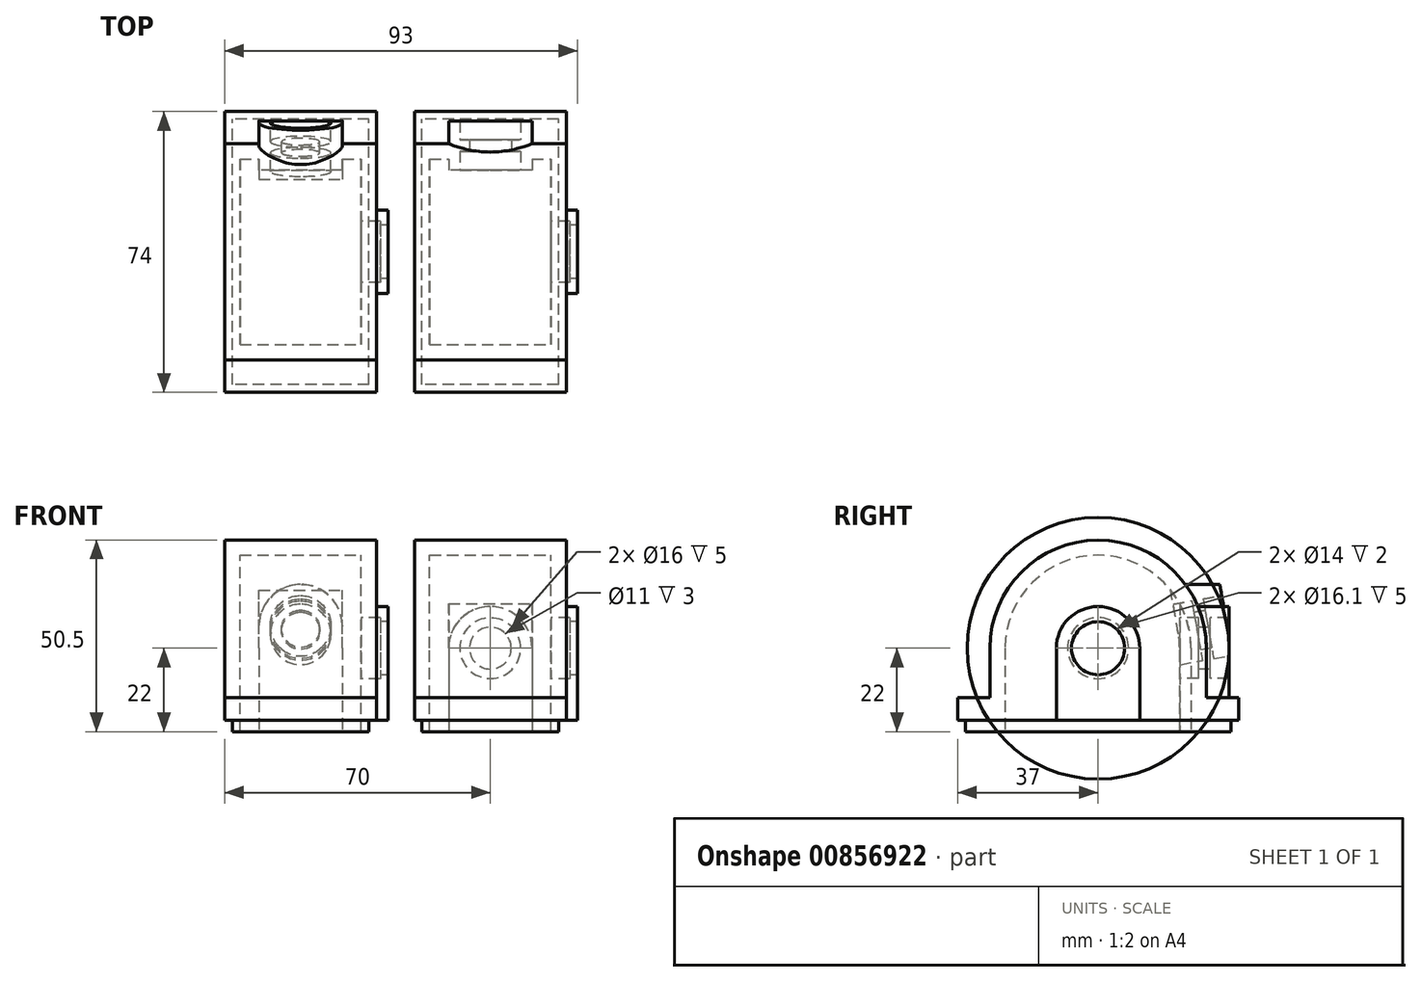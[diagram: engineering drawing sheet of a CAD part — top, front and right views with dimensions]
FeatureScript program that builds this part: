
annotation { "Feature Type Name" : "Feature", "Feature Type Description" : "" }
export const myFeature = defineFeature(function(context is Context, id is Id, definition is map)
    precondition{}
    {
        {
            var Q0;
            Q0=qCreatedBy(makeId("Right.planeOp"),FACE);
            var sketch = newSketch(context, id + "F0", { "sketchPlane" : qUnion([Q0])});
            skArc(sketch, "E0", {"start": v(28.5, 22) * mm, "mid": v(0, 50.5) * mm, "end": v(-28.5, 22) * mm});
            skLineSegment(sketch, "E1", {"start": v(-28.5, 22) * mm, "end": v(28.5, 22) * mm, "construction": true});
            skLineSegment(sketch, "E2", {"start": v(-28.5, 22) * mm, "end": v(-28.5, 9) * mm});
            skLineSegment(sketch, "E3", {"start": v(28.5, 22) * mm, "end": v(28.5, 9) * mm});
            skLineSegment(sketch, "E4.top", {"start": v(37, 9) * mm, "end": v(28.5, 9) * mm});
            skLineSegment(sketch, "E4.left", {"start": v(37, 0) * mm, "end": v(37, 9) * mm});
            skLineSegment(sketch, "E4.right", {"start": v(-37, 0) * mm, "end": v(-37, 9) * mm});
            skPoint(sketch, "E4.middle", {"position": v(0, 4.5) * mm});
            skLineSegment(sketch, "E5.trimOffspring", {"start": v(-28.5, 9) * mm, "end": v(-37, 9) * mm});
            skLineSegment(sketch, "E6", {"start": v(-37, 0) * mm, "end": v(37, 0) * mm});
            skSolve(sketch);
        }
        {
            var Q0;
            Q0 = qSketchRegion(id + "F0", true);
            extrude(context, id + "F1", {"entities" : qUnion([Q0]), "depth" : 40 * mm, "offsetDistance" : 25 * mm, "symmetric" : true});
        }
        {
            var Q0;
            Q0=qCreatedBy(makeId("Right.planeOp"),FACE);
            var sketch = newSketch(context, id + "F2", { "sketchPlane" : qUnion([Q0])});
            skArc(sketch, "E7", {"start": v(24.5, 22) * mm, "mid": v(0, 46.5) * mm, "end": v(-24.5, 22) * mm});
            skLineSegment(sketch, "E8", {"start": v(-24.5, 22) * mm, "end": v(24.5, 22) * mm, "construction": true});
            skLineSegment(sketch, "E9", {"start": v(-24.5, 22) * mm, "end": v(-24.5, 0) * mm});
            skLineSegment(sketch, "E10", {"start": v(-24.5, 0) * mm, "end": v(24.5, 0) * mm});
            skLineSegment(sketch, "E11", {"start": v(24.5, 0) * mm, "end": v(24.5, 22) * mm});
            skSolve(sketch);
        }
        {
            var Q0;
            Q0 = qSketchRegion(id + "F2", true);
            extrude(context, id + "F3", {"entities" : qUnion([Q0]), "operationType" : NewBodyOperationType.REMOVE, "oppositeDirection" : true, "depth" : 32 * mm, "offsetDistance" : 25 * mm, "symmetric" : true});
        }
        {
            var Q0;
            Q0=makeQuery(id+"F1.opExtrude","CAP_FACE",FACE,{"disambiguationData":[OSD([sQuery(id+"F0.wireOp",EDGE,"E0"),sQuery(id+"F0.wireOp",EDGE,"E2"),sQuery(id+"F0.wireOp",EDGE,"E3"),sQuery(id+"F0.wireOp",EDGE,"E4.top"),sQuery(id+"F0.wireOp",EDGE,"E4.left"),sQuery(id+"F0.wireOp",EDGE,"E4.right"),sQuery(id+"F0.wireOp",EDGE,"E5.trimOffspring"),sQuery(id+"F0.wireOp",EDGE,"E6")])],"isStart":false});
            var sketch = newSketch(context, id + "F4", { "sketchPlane" : qUnion([Q0])});
            skArc(sketch, "E12", {"start": v(11, 22) * mm, "mid": v(0, 33) * mm, "end": v(-11, 22) * mm});
            skLineSegment(sketch, "E13", {"start": v(-11, 22) * mm, "end": v(-11, 0) * mm});
            skLineSegment(sketch, "E14", {"start": v(-11, 0) * mm, "end": v(11, 0) * mm});
            skLineSegment(sketch, "E15", {"start": v(11, 0) * mm, "end": v(11, 22) * mm});
            skSolve(sketch);
        }
        {
            var Q0;
            Q0 = qSketchRegion(id + "F4", true);
            extrude(context, id + "F5", {"entities" : qUnion([Q0]), "operationType" : NewBodyOperationType.ADD, "depth" : 3 * mm, "offsetDistance" : 25 * mm});
        }
        {
            var Q0;
            Q0=qCreatedBy(makeId("Front.planeOp"),FACE);
            var sketch = newSketch(context, id + "F6", { "sketchPlane" : qUnion([Q0])});
            skLineSegment(sketch, "E16", {"start": v(42.03, 22) * mm, "end": v(7.34, 22) * mm, "construction": true});
            skLineSegment(sketch, "E17", {"start": v(16, 22) * mm, "end": v(16, 30.05) * mm});
            skLineSegment(sketch, "E18", {"start": v(16, 30.05) * mm, "end": v(21, 30.05) * mm});
            skLineSegment(sketch, "E19", {"start": v(21, 30.05) * mm, "end": v(21, 29) * mm});
            skLineSegment(sketch, "E20", {"start": v(21, 29) * mm, "end": v(23, 29) * mm});
            skLineSegment(sketch, "E21", {"start": v(23, 29) * mm, "end": v(23, 22) * mm});
            skLineSegment(sketch, "E22", {"start": v(23, 22) * mm, "end": v(16, 22) * mm});
            skLineSegment(sketch, "E23", {"start": v(16, 22) * mm, "end": v(23, 22) * mm});
            skSolve(sketch);
        }
        {
            var Q0;
            Q0 = qSketchRegion(id + "F6", true);
            var Q1;
            Q1=sQuery(id+"F6.wireOp",EDGE,"E16");
            revolve(context, id + "F7", {"operationType" : NewBodyOperationType.REMOVE, "surfaceOperationType" : NewSurfaceOperationType.NEW, "entities" : qUnion([Q0]), "axis" : qUnion([Q1]), "revolveType" : RevolveType.FULL, "oppositeDirection" : true});
        }
        {
            var Q0;
            {var subQ0=sQuery(id+"F4.wireOp",EDGE,"E14");Q0=makeQuery(id+"Fj3ByAB7jm97h4G_1.1.F5.boolean.opBoolean","MERGE",FACE,{"derivedFrom":[makeQuery(id+"F5.boolean.opBoolean","MERGE",FACE,{"derivedFrom":[makeQuery(id+"F1.opExtrude","SWEPT_FACE",FACE,{"disambiguationData":[OSD([sQuery(id+"F0.wireOp",EDGE,"E6")])]}),makeQuery(id+"F5.opExtrude","SWEPT_FACE",FACE,{"disambiguationData":[OSD([subQ0])]})]}),makeQuery(id+"Fj3ByAB7jm97h4G_1.1.F5.opExtrude","SWEPT_FACE",FACE,{"disambiguationData":[OSD([subQ0])]})]});}
            var sketch = newSketch(context, id + "F8", { "sketchPlane" : qUnion([Q0])});
            skLineSegment(sketch, "E24.bottom", {"start": v(18, 35) * mm, "end": v(-18, 35) * mm});
            skLineSegment(sketch, "E24.top", {"start": v(18, -35) * mm, "end": v(-18, -35) * mm});
            skLineSegment(sketch, "E24.left", {"start": v(18, 35) * mm, "end": v(18, -35) * mm});
            skLineSegment(sketch, "E24.right", {"start": v(-18, 35) * mm, "end": v(-18, -35) * mm});
            skPoint(sketch, "E24.middle", {"position": v(0, 0) * mm});
            skLineSegment(sketch, "E25.0.0", {"start": v(-20, 37) * mm, "end": v(-20, 11) * mm});
            skLineSegment(sketch, "E25.0.1", {"start": v(-20, 11) * mm, "end": v(-23, 11) * mm});
            skLineSegment(sketch, "E25.0.2", {"start": v(-23, 11) * mm, "end": v(-23, -11) * mm});
            skLineSegment(sketch, "E25.0.3", {"start": v(-23, -11) * mm, "end": v(-20, -11) * mm});
            skLineSegment(sketch, "E25.0.4", {"start": v(-20, -11) * mm, "end": v(-20, -37) * mm});
            skLineSegment(sketch, "E25.0.5", {"start": v(-20, -37) * mm, "end": v(20, -37) * mm});
            skLineSegment(sketch, "E25.0.6", {"start": v(20, -37) * mm, "end": v(20, -11) * mm});
            skLineSegment(sketch, "E25.0.7", {"start": v(20, -11) * mm, "end": v(23, -11) * mm});
            skLineSegment(sketch, "E25.0.8", {"start": v(23, -11) * mm, "end": v(23, 11) * mm});
            skLineSegment(sketch, "E25.0.9", {"start": v(23, 11) * mm, "end": v(20, 11) * mm});
            skLineSegment(sketch, "E25.0.10", {"start": v(20, 11) * mm, "end": v(20, 37) * mm});
            skLineSegment(sketch, "E25.0.11", {"start": v(20, 37) * mm, "end": v(-20, 37) * mm});
            skSolve(sketch);
        }
        {
            var Q0;
            Q0 = qSketchRegion(id + "F8", true);
            extrude(context, id + "F9", {"entities" : qUnion([Q0]), "operationType" : NewBodyOperationType.REMOVE, "oppositeDirection" : true, "depth" : 3 * mm, "offsetDistance" : 25 * mm});
        }
        {
            var Q0;
            Q0=makeQuery(id+"F1.opExtrude","SWEPT_BODY",BODY,{"disambiguationData":[OSD([sQuery(id+"F0.wireOp",EDGE,"E0"),sQuery(id+"F0.wireOp",EDGE,"E2"),sQuery(id+"F0.wireOp",EDGE,"E3"),sQuery(id+"F0.wireOp",EDGE,"E4.top"),sQuery(id+"F0.wireOp",EDGE,"E4.left"),sQuery(id+"F0.wireOp",EDGE,"E4.right"),sQuery(id+"F0.wireOp",EDGE,"E5.trimOffspring"),sQuery(id+"F0.wireOp",EDGE,"E6")])]});
            transform(context, id + "F10", {"entities" : qUnion([Q0]), "transformType" : TransformType.TRANSLATION_3D, "dx" : 50 * mm, "dy" : 0 * mm, "dz" : 0 * mm, "makeCopy" : true});
        }
        {
            var Q0;
            Q0=makeQuery(id+"F10.opPattern","COPY",FACE,{"derivedFrom":makeQuery(id+"F1.opExtrude","CAP_FACE",FACE,{"disambiguationData":[OSD([sQuery(id+"F0.wireOp",EDGE,"E0"),sQuery(id+"F0.wireOp",EDGE,"E2"),sQuery(id+"F0.wireOp",EDGE,"E3"),sQuery(id+"F0.wireOp",EDGE,"E4.top"),sQuery(id+"F0.wireOp",EDGE,"E4.left"),sQuery(id+"F0.wireOp",EDGE,"E4.right"),sQuery(id+"F0.wireOp",EDGE,"E5.trimOffspring"),sQuery(id+"F0.wireOp",EDGE,"E6")])],"isStart":false}),"instanceName":"1"});
            var Q1;
            Q1=makeQuery(id+"F10.opPattern","COPY",FACE,{"derivedFrom":makeQuery(id+"F1.opExtrude","CAP_FACE",FACE,{"disambiguationData":[OSD([sQuery(id+"F0.wireOp",EDGE,"E0"),sQuery(id+"F0.wireOp",EDGE,"E2"),sQuery(id+"F0.wireOp",EDGE,"E3"),sQuery(id+"F0.wireOp",EDGE,"E4.top"),sQuery(id+"F0.wireOp",EDGE,"E4.left"),sQuery(id+"F0.wireOp",EDGE,"E4.right"),sQuery(id+"F0.wireOp",EDGE,"E5.trimOffspring"),sQuery(id+"F0.wireOp",EDGE,"E6")])],"isStart":true}),"instanceName":"1"});
            cPlane(context, id + "F11", {"entities" : qUnion([Q0, Q1]), "cplaneType" : CPlaneType.MID_PLANE, "offset" : 25 * mm, "width" : 150 * mm, "height" : 150 * mm});
        }
        {
            var Q0;
            Q0=qCreatedBy(id+"F11.planeOp",FACE);
            var sketch = newSketch(context, id + "F12", { "sketchPlane" : qUnion([Q0])});
            skLineSegment(sketch, "E26", {"start": v(21.5, 0) * mm, "end": v(21.5, 33) * mm});
            skLineSegment(sketch, "E27", {"start": v(24.84, 33) * mm, "end": v(34.5, 33) * mm});
            skLineSegment(sketch, "E28", {"start": v(34.5, 33) * mm, "end": v(34.5, 0) * mm});
            skLineSegment(sketch, "E29", {"start": v(34.5, 0) * mm, "end": v(21.5, 0) * mm});
            skLineSegment(sketch, "E30", {"start": v(24.84, 33) * mm, "end": v(21.5, 34) * mm});
            skLineSegment(sketch, "E31", {"start": v(21.5, 34) * mm, "end": v(21.5, 33) * mm});
            skSolve(sketch);
        }
        {
            var Q0;
            Q0 = qSketchRegion(id + "F12", true);
            extrude(context, id + "F13", {"entities" : qUnion([Q0]), "operationType" : NewBodyOperationType.ADD, "depth" : 22 * mm, "offsetDistance" : 25 * mm, "symmetric" : true});
        }
        {
            var Q0;
            {var subQ1=sQuery(id+"F12.wireOp",EDGE,"E27");Q0=makeQuery(id+"F13.boolean.opBoolean","SPLIT",EDGE,{"disambiguationData":[TD([makeQuery(id+"F10.opPattern","COPY",FACE,{"derivedFrom":makeQuery(id+"F1.opExtrude","SWEPT_FACE",FACE,{"disambiguationData":[OSD([sQuery(id+"F0.wireOp",EDGE,"E0")])]}),"instanceName":"1"})])],"derivedFrom":makeQuery(id+"F13.opExtrude","CAP_EDGE",EDGE,{"disambiguationData":[OSD([subQ1])],"isStart":false})});}
            var Q1;
            {var subQ1=sQuery(id+"F12.wireOp",EDGE,"E27");Q1=makeQuery(id+"F13.boolean.opBoolean","SPLIT",EDGE,{"disambiguationData":[TD([makeQuery(id+"F10.opPattern","COPY",FACE,{"derivedFrom":makeQuery(id+"F1.opExtrude","SWEPT_FACE",FACE,{"disambiguationData":[OSD([sQuery(id+"F0.wireOp",EDGE,"E0")])]}),"instanceName":"1"})])],"derivedFrom":makeQuery(id+"F13.opExtrude","CAP_EDGE",EDGE,{"disambiguationData":[OSD([subQ1])],"isStart":true})});}
            fillet(context, id + "F14", {"entities" : qUnion([Q0, Q1]), "radius" : 11 * mm, "tangentPropagation" : true, "allowEdgeOverflow" : false});
        }
        {
            var Q0;
            Q0=qCreatedBy(id+"F11.planeOp",FACE);
            var sketch = newSketch(context, id + "F15", { "sketchPlane" : qUnion([Q0])});
            skCircle(sketch, "E32.0", {"center": v(0, 22) * mm, "radius": 7 * mm, "construction": true});
            skLineSegment(sketch, "E33", {"start": v(0, 22) * mm, "end": v(49.84, 22) * mm, "construction": true});
            skLineSegment(sketch, "E34", {"start": v(21.5, 22) * mm, "end": v(21.5, 30) * mm});
            skLineSegment(sketch, "E35", {"start": v(21.5, 30) * mm, "end": v(26.5, 30) * mm});
            skLineSegment(sketch, "E36", {"start": v(26.5, 30) * mm, "end": v(26.5, 27.5) * mm});
            skLineSegment(sketch, "E37", {"start": v(26.5, 27.5) * mm, "end": v(29.5, 27.5) * mm});
            skLineSegment(sketch, "E38", {"start": v(29.5, 27.5) * mm, "end": v(29.5, 30) * mm});
            skLineSegment(sketch, "E39", {"start": v(29.5, 30) * mm, "end": v(34.5, 30) * mm});
            skLineSegment(sketch, "E40", {"start": v(34.5, 30) * mm, "end": v(34.5, 22) * mm});
            skLineSegment(sketch, "E41.0", {"start": v(34.5, 22) * mm, "end": v(34.5, 33) * mm, "construction": true});
            skLineSegment(sketch, "E42.0", {"start": v(21.5, 0) * mm, "end": v(21.5, 0) * mm});
            skLineSegment(sketch, "E43", {"start": v(21.5, 22) * mm, "end": v(34.5, 22) * mm});
            skSolve(sketch);
        }
        {
            var Q0;
            Q0 = qSketchRegion(id + "F15", true);
            var Q1;
            Q1=sQuery(id+"F15.wireOp",EDGE,"E33");
            revolve(context, id + "F16", {"operationType" : NewBodyOperationType.REMOVE, "surfaceOperationType" : NewSurfaceOperationType.NEW, "entities" : qUnion([Q0]), "axis" : qUnion([Q1]), "revolveType" : RevolveType.FULL});
        }
        {
            var Q0;
            Q0=qCreatedBy(makeId("Right.planeOp"),FACE);
            var sketch = newSketch(context, id + "F17", { "sketchPlane" : qUnion([Q0])});
            skCircle(sketch, "E44.0", {"center": v(0, 22) * mm, "radius": 7 * mm, "construction": true});
            skLineSegment(sketch, "E45", {"start": v(0, 22) * mm, "end": v(36.47, 22) * mm, "construction": true});
            skLineSegment(sketch, "E46", {"start": v(0, 22) * mm, "end": v(42.78, 29.54) * mm, "construction": true});
            skLineSegment(sketch, "E47", {"start": v(21.5, 0) * mm, "end": v(21.5, 22) * mm});
            skLineSegment(sketch, "E48", {"start": v(34.5, 0) * mm, "end": v(34.5, 22) * mm});
            skArc(sketch, "E49", {"start": v(21.5, 22) * mm, "mid": v(21.42, 23.87) * mm, "end": v(21.17, 25.73) * mm});
            skArc(sketch, "E50", {"start": v(34.5, 22) * mm, "mid": v(34.37, 25) * mm, "end": v(33.98, 28) * mm});
            skLineSegment(sketch, "E51", {"start": v(32.07, 38.82) * mm, "end": v(16.28, 36.04) * mm, "construction": true});
            skLineSegment(sketch, "E52", {"start": v(33.98, 28) * mm, "end": v(32.07, 38.82) * mm});
            skLineSegment(sketch, "E53", {"start": v(0, 22) * mm, "end": v(0, 50.5) * mm, "construction": true});
            skLineSegment(sketch, "E54", {"start": v(21.5, 0) * mm, "end": v(34.5, 0) * mm});
            skLineSegment(sketch, "E55", {"start": v(32.07, 38.82) * mm, "end": v(18.87, 38.82) * mm});
            skLineSegment(sketch, "E56", {"start": v(21.17, 25.73) * mm, "end": v(18.87, 38.82) * mm});
            skPoint(sketch, "E57.orphan", {"position": v(0, 38.82) * mm});
            skSolve(sketch);
        }
        {
            var Q0;
            Q0=makeQuery(id+"F17.imprint","IMPRINT",FACE,{"disambiguationData":[TD([[makeQuery(id+"F17.imprint","IMPRINT",EDGE,{"derivedFrom":sQuery(id+"F17.wireOp",EDGE,"E47")}),-1.0]])]});
            extrude(context, id + "F18", {"entities" : qUnion([Q0]), "operationType" : NewBodyOperationType.ADD, "depth" : 22 * mm, "offsetDistance" : 25 * mm, "symmetric" : true});
        }
        {
            var Q0;
            Q0=qCreatedBy(makeId("Right.planeOp"),FACE);
            var sketch = newSketch(context, id + "F19", { "sketchPlane" : qUnion([Q0])});
            skLineSegment(sketch, "E58.0", {"start": v(0, 22) * mm, "end": v(42.78, 29.54) * mm, "construction": true});
            skLineSegment(sketch, "E59.0", {"start": v(33.98, 28) * mm, "end": v(32.07, 38.82) * mm, "construction": true});
            skLineSegment(sketch, "E60", {"start": v(28.18, 32.05) * mm, "end": v(27.66, 35) * mm});
            skLineSegment(sketch, "E61", {"start": v(27.66, 35) * mm, "end": v(32.59, 35.87) * mm});
            skLineSegment(sketch, "E62", {"start": v(32.59, 35.87) * mm, "end": v(33.98, 28) * mm});
            skLineSegment(sketch, "E63", {"start": v(21.17, 25.73) * mm, "end": v(33.98, 28) * mm});
            skLineSegment(sketch, "E64", {"start": v(24.7, 34.48) * mm, "end": v(25.23, 31.53) * mm});
            skLineSegment(sketch, "E65", {"start": v(25.23, 31.53) * mm, "end": v(28.18, 32.05) * mm});
            skLineSegment(sketch, "E66", {"start": v(24.7, 34.48) * mm, "end": v(19.78, 33.61) * mm});
            skLineSegment(sketch, "E67", {"start": v(19.78, 33.61) * mm, "end": v(21.17, 25.73) * mm, "construction": true});
            skLineSegment(sketch, "E68", {"start": v(19.78, 33.61) * mm, "end": v(16.83, 33.1) * mm});
            skLineSegment(sketch, "E69", {"start": v(16.83, 33.1) * mm, "end": v(18.22, 25.21) * mm});
            skLineSegment(sketch, "E70", {"start": v(18.22, 25.21) * mm, "end": v(21.17, 25.73) * mm});
            skSolve(sketch);
        }
        {
            var Q0;
            Q0 = qSketchRegion(id + "F19", true);
            var Q1;
            Q1=sQuery(id+"F19.wireOp",EDGE,"E58.0");
            revolve(context, id + "F20", {"operationType" : NewBodyOperationType.REMOVE, "surfaceOperationType" : NewSurfaceOperationType.NEW, "entities" : qUnion([Q0]), "axis" : qUnion([Q1]), "revolveType" : RevolveType.FULL, "oppositeDirection" : true});
        }
        {
            var Q0;
            Q0=makeQuery(id+"F18.opExtrude","CAP_EDGE",EDGE,{"disambiguationData":[OSD([sQuery(id+"F17.wireOp",EDGE,"E55")])],"isStart":true});
            var Q1;
            Q1=makeQuery(id+"F18.opExtrude","CAP_EDGE",EDGE,{"disambiguationData":[OSD([sQuery(id+"F17.wireOp",EDGE,"E55")])],"isStart":false});
            fillet(context, id + "F21", {"entities" : qUnion([Q0, Q1]), "radius" : 11 * mm, "tangentPropagation" : true, "allowEdgeOverflow" : false});
        }
    });
